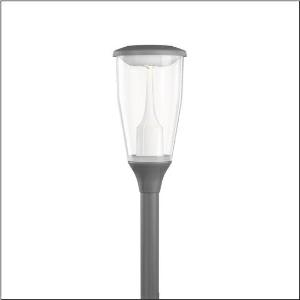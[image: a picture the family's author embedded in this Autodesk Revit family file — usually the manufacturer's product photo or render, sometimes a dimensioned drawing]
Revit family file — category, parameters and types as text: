
# Revit family: dl_11_iq___p1_0a_5xa5565lf14h000022_286d
name_source: partatom
category: Lighting Fixtures
units: mm (PartAtom-declared; Revit-internal decimal feet)

## family parameters
Cut with Voids When Loaded = No
Host = Face
Light Source = No
Part Type = Normal
Room Calculation Point = No
Round Connector Dimension = Use Diameter
Shared = No

## types (1)
- --- (1 x LED, 1530 lm, 10 W, 4000K)
    Apparent Load = 10 VA
    CIE Flux Codes = 34 63 91 95 100
    Color Rendering = 70
    Color Temperature = 4000K
    Default Elevation = 1800 mm
    Description = DL 11 iQ, mast luminaire, Module 540 iQ-SR, primary light control with 3 zone facetted reflector, of plastic, silver coated, highly specular, structured, primary optical cover: cover, of PMMA, transparent, light distribution: P1.0a, light emission: direct distribution, primary light characteristic: asymmetric, installation type: post-top, LED, High Power LED, rated luminous flux: 1.560lm, luminous efficacy: 149lm/W, light colour: 740, colour temperature: 4000K, control: Street-Remote, Auto-Match, Temp-Guard, Lumen-Switch, Night-Set, Smart-Wire, Light-Fading, Desk-Remote (wireless, voltage-free reading and setting of iQ features in the workshop via application-optimized NFC function/RFID function), optimised constant luminous flux control (CLO 2.0), mains connection: 220..240V, AC, 50/60Hz, connection cable pre-assembled, cable length: 5,5m, start of lifetime: 10W, end of service life: 10W, reduction: 5W, luminaire housing, upper part, of diecast aluminium, coated, Siteco® metallic grey (DB 702S), spigot size: 60mm (post-top), post-top mast mounting element, of diecast aluminium, coated, Siteco® metallic grey (DB 702S), Module 540 iQ-SR, traffic white (RAL 9016), equipment: standard, protection rating (complete): IP66, insulation class (complete): insulation class II (safety insulation), certification: CE, ENEC, ENEC+, VDE, packaging unit: 1 piece

Light Distribution: P1.0a
    Height = 665 mm
    Lamp = 1 x LED
    Lamp Light Flux = 1530 lm
    Lamp Power = 10 W
    Lamp count = 1
    Length = 334 mm
    Luminous efficacy = 153 lm/W
    Manufacturer = Siteco
    ModVariant = No
    Model = 5XA5565LF14H000022
    Number of Poles = 1
    OnlyDefault = Yes
    Power Factor = 1
    Product Name = DL 11 iQ | P1.0a
    Product group = mast luminaire | pylon top
    ProductGroupID = 6100
    Protection Class = Protection class II
    Protection Degree = IP 66
    RLX_Detail_Level = 1
    RLX_Emergency_Light_Flux = 0 lm
    RLX_Emergency_Type = 0
    RLX_Emergency_Type_DB = No
    RlxData = <blob elided: 107697 chars, md5=658522f1>
    Socket = socket
    Standby Power = 0 W
    System Light Flux = 1530 lm
    System Power = 10 W
    Type Comments = factory setting: luminous flux: 100 % | dim-lin: 254 | 401 mA
    Type Image = l_1258354.jpg
    URL = http://relux.com
    VarID = @adj_042405
    Voltage = 0 V
    Weight = 0.00 kg
    Width = 0 mm  [stored 0 ft]

note: [stored X ft] marks values corroborated as IEEE doubles in the binary element streams (Revit-internal decimal feet)

## geometry (parser evidence)
native form markers: Blend x4, Sweep x11
no freeform markers — native parametric forms only
